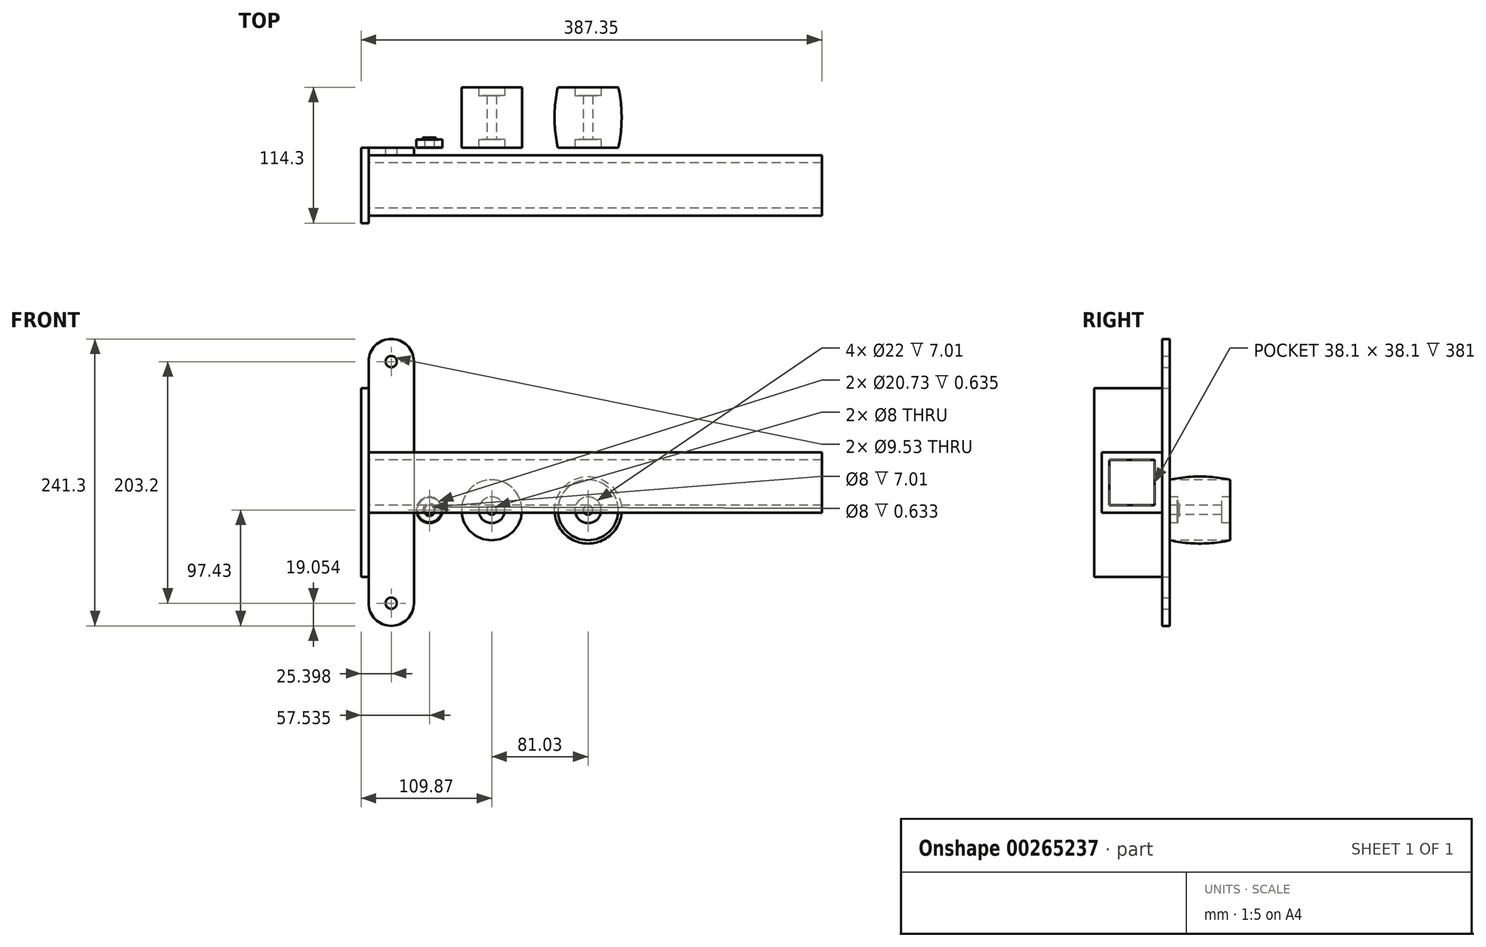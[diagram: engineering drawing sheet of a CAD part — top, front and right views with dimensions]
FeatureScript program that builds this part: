
annotation { "Feature Type Name" : "Feature", "Feature Type Description" : "" }
export const myFeature = defineFeature(function(context is Context, id is Id, definition is map)
    precondition{}
    {
        {
            var Q0;
            Q0=qCreatedBy(makeId("Front.planeOp"),FACE);
            var sketch = newSketch(context, id + "F0", { "sketchPlane" : qUnion([Q0])});
            skLineSegment(sketch, "E0.right", {"start": v(-109.87, -56.15) * mm, "end": v(-109.87, 102.6) * mm});
            skLineSegment(sketch, "E1.left", {"start": v(-109.87, 102.6) * mm, "end": v(-109.87, -56.15) * mm});
            skLineSegment(sketch, "E1.right", {"start": v(-103.52, 102.6) * mm, "end": v(-103.52, -56.15) * mm});
            skLineSegment(sketch, "E2", {"start": v(-103.52, 102.6) * mm, "end": v(-109.87, 102.6) * mm});
            skLineSegment(sketch, "E3", {"start": v(-103.52, -56.15) * mm, "end": v(-109.87, -56.15) * mm});
            skArc(sketch, "E4", {"start": v(-65.42, 124.82) * mm, "mid": v(-84.47, 143.87) * mm, "end": v(-103.52, 124.82) * mm});
            skLineSegment(sketch, "E5", {"start": v(-103.52, 102.6) * mm, "end": v(-103.52, 124.82) * mm});
            skArc(sketch, "E6", {"start": v(-103.52, -78.38) * mm, "mid": v(-84.47, -97.43) * mm, "end": v(-65.42, -78.38) * mm});
            skLineSegment(sketch, "E7", {"start": v(-103.52, -56.15) * mm, "end": v(-103.52, -78.38) * mm});
            skLineSegment(sketch, "E8", {"start": v(-65.42, 124.82) * mm, "end": v(-65.42, -78.38) * mm});
            skSolve(sketch);
        }
        {
            var Q0;
            Q0=makeQuery(id+"F0.imprint","IMPRINT",FACE,{"disambiguationData":[TD([[makeQuery(id+"F0.imprint","IMPRINT",EDGE,{"derivedFrom":sQuery(id+"F0.wireOp",EDGE,"E1.right")}),-1.0]])]});
            extrude(context, id + "F1", {"entities" : qUnion([Q0]), "depth" : 63.5 * mm});
        }
        {
            var Q0;
            Q0=makeQuery(id+"F0.imprint","IMPRINT",FACE,{"disambiguationData":[TD([[makeQuery(id+"F0.imprint","IMPRINT",EDGE,{"derivedFrom":sQuery(id+"F0.wireOp",EDGE,"E1.right")}),1.0]])]});
            extrude(context, id + "F2", {"entities" : qUnion([Q0]), "operationType" : NewBodyOperationType.ADD, "depth" : 6.35 * mm});
        }
        {
            var Q0;
            Q0=sQuery(id+"F0.wireOp",VERTEX,"E6.center");
            var Q1;
            Q1=sQuery(id+"F0.wireOp",VERTEX,"E4.center");
            var Q2;
            Q2=makeQuery(id+"F1.opExtrude","SWEPT_BODY",BODY,{"disambiguationData":[OSD([sQuery(id+"F0.wireOp",EDGE,"E1.bottom"),sQuery(id+"F0.wireOp",EDGE,"E1.top"),sQuery(id+"F0.wireOp",EDGE,"E1.left"),sQuery(id+"F0.wireOp",EDGE,"E1.right")])]});
            hole(context, id + "F3", {"style" : HoleStyle.SIMPLE, "endStyle" : HoleEndStyle.THROUGH, "oppositeDirection" : true, "holeDiameter" : 9.52 * mm, "tappedDepth" : 12.7 * mm, "tapClearance" : 3, "startFromSketch" : true, "locations" : qUnion([Q0, Q1]), "scope" : qUnion([Q2])});
        }
        {
            var Q0;
            Q0=makeQuery(id+"F1.opExtrude","SWEPT_FACE",FACE,{"disambiguationData":[OSD([sQuery(id+"F0.wireOp",EDGE,"E1.right")])]});
            var sketch = newSketch(context, id + "F4", { "sketchPlane" : qUnion([Q0])});
            skLineSegment(sketch, "E9.bottom", {"start": v(-6.35, 48.62) * mm, "end": v(-57.15, 48.62) * mm});
            skLineSegment(sketch, "E9.top", {"start": v(-6.35, -2.18) * mm, "end": v(-57.15, -2.18) * mm});
            skLineSegment(sketch, "E9.left", {"start": v(-6.35, 48.62) * mm, "end": v(-6.35, -2.18) * mm});
            skLineSegment(sketch, "E9.right", {"start": v(-57.15, 48.62) * mm, "end": v(-57.15, -2.18) * mm});
            skLineSegment(sketch, "E10.0", {"start": v(-50.8, 42.27) * mm, "end": v(-50.8, 4.17) * mm});
            skLineSegment(sketch, "E10.1", {"start": v(-12.7, 42.27) * mm, "end": v(-50.8, 42.27) * mm});
            skLineSegment(sketch, "E10.2", {"start": v(-12.7, 42.27) * mm, "end": v(-12.7, 4.17) * mm});
            skLineSegment(sketch, "E10.3", {"start": v(-12.7, 4.17) * mm, "end": v(-50.8, 4.17) * mm});
            skSolve(sketch);
        }
        {
            var Q0;
            Q0 = qSketchRegion(id + "F4", true);
            extrude(context, id + "F5", {"entities" : qUnion([Q0]), "operationType" : NewBodyOperationType.ADD, "depth" : 381 * mm});
        }
        {
            var Q0;
            Q0=qCreatedBy(makeId("Top.planeOp"),FACE);
            var sketch = newSketch(context, id + "F6", { "sketchPlane" : qUnion([Q0])});
            skLineSegment(sketch, "E11", {"start": v(0, 0) * mm, "end": v(0, 108.82) * mm, "construction": true});
            skLineSegment(sketch, "E12", {"start": v(-25.4, 0) * mm, "end": v(-25.4, 50.8) * mm});
            skLineSegment(sketch, "E13", {"start": v(-4, 7.01) * mm, "end": v(-4, 43.79) * mm});
            skLineSegment(sketch, "E14", {"start": v(-11, 0) * mm, "end": v(-11, 7.01) * mm});
            skLineSegment(sketch, "E15", {"start": v(-25.4, 0) * mm, "end": v(-11, 0) * mm});
            skLineSegment(sketch, "E16", {"start": v(-11, 7.01) * mm, "end": v(-4, 7.01) * mm});
            skLineSegment(sketch, "E17", {"start": v(-25.4, 50.8) * mm, "end": v(-11, 50.8) * mm});
            skLineSegment(sketch, "E18", {"start": v(-11, 43.79) * mm, "end": v(-4, 43.79) * mm});
            skPoint(sketch, "E19.orphan", {"position": v(-4, 0) * mm});
            skLineSegment(sketch, "E20.trimOffspring", {"start": v(-11, 43.79) * mm, "end": v(-11, 50.8) * mm});
            skSolve(sketch);
        }
        {
            var Q0;
            Q0 = qSketchRegion(id + "F6", true);
            var Q1;
            Q1=sQuery(id+"F6.wireOp",EDGE,"E11");
            revolve(context, id + "F7", {"entities" : qUnion([Q0]), "axis" : qUnion([Q1]), "revolveType" : RevolveType.FULL});
        }
        {
            var Q0;
            Q0=qCreatedBy(makeId("Top.planeOp"),FACE);
            var sketch = newSketch(context, id + "F8", { "sketchPlane" : qUnion([Q0])});
            skLineSegment(sketch, "E21", {"start": v(81.03, 0) * mm, "end": v(81.03, 50.8) * mm, "construction": true});
            skLineSegment(sketch, "E22", {"start": v(55.63, 0) * mm, "end": v(55.63, 50.8) * mm, "construction": true});
            skLineSegment(sketch, "E23", {"start": v(55.63, 0) * mm, "end": v(70.03, 0) * mm});
            skLineSegment(sketch, "E24", {"start": v(55.63, 50.8) * mm, "end": v(70.03, 50.8) * mm});
            skPoint(sketch, "E25.orphan", {"position": v(55.63, 70.87) * mm});
            skPoint(sketch, "E26.orphan", {"position": v(81.03, 70.87) * mm});
            skPoint(sketch, "E27.endSnap0", {"position": v(81.03, 25.4) * mm});
            skArc(sketch, "E28", {"start": v(55.63, 50.8) * mm, "mid": v(52.84, 25.4) * mm, "end": v(55.63, 0) * mm});
            skPoint(sketch, "E28.third.point", {"position": v(286.5, 28.62) * mm});
            skPoint(sketch, "E29.orphan", {"position": v(55.63, 25.4) * mm});
            skLineSegment(sketch, "E30", {"start": v(70.03, 7.01) * mm, "end": v(77.03, 7.01) * mm});
            skLineSegment(sketch, "E31", {"start": v(77.03, 7.01) * mm, "end": v(77.03, 43.79) * mm});
            skLineSegment(sketch, "E32", {"start": v(77.03, 43.79) * mm, "end": v(70.03, 43.79) * mm});
            skLineSegment(sketch, "E33", {"start": v(70.03, 50.8) * mm, "end": v(70.03, 43.79) * mm});
            skPoint(sketch, "E34.orphan", {"position": v(68.33, 43.79) * mm});
            skPoint(sketch, "E35.orphan", {"position": v(68.33, 7.01) * mm});
            skLineSegment(sketch, "E36.trimOffspring", {"start": v(70.03, 7.01) * mm, "end": v(70.03, 0) * mm});
            skPoint(sketch, "E37.orphan", {"position": v(68.33, 50.8) * mm});
            skPoint(sketch, "E38.orphan", {"position": v(68.33, 0) * mm});
            skSolve(sketch);
        }
        {
            var Q0;
            Q0 = qSketchRegion(id + "F8", true);
            var Q1;
            Q1=sQuery(id+"F8.wireOp",EDGE,"E21");
            revolve(context, id + "F9", {"entities" : qUnion([Q0]), "axis" : qUnion([Q1]), "revolveType" : RevolveType.FULL});
        }
        {
            var Q0;
            Q0=qCreatedBy(makeId("Top.planeOp"),FACE);
            var sketch = newSketch(context, id + "F10", { "sketchPlane" : qUnion([Q0])});
            skLineSegment(sketch, "E39", {"start": v(-52.34, 0) * mm, "end": v(-52.34, 11.8) * mm, "construction": true});
            skLineSegment(sketch, "E40", {"start": v(-56.34, 0) * mm, "end": v(-56.34, 7.01) * mm});
            skLineSegment(sketch, "E41", {"start": v(-63.33, 0) * mm, "end": v(-63.33, 7.01) * mm});
            skLineSegment(sketch, "E42", {"start": v(-63.33, 0) * mm, "end": v(-62.7, 0) * mm});
            skLineSegment(sketch, "E43", {"start": v(-62.7, 0) * mm, "end": v(-62.7, 0.63) * mm});
            skLineSegment(sketch, "E44", {"start": v(-62.7, 0.63) * mm, "end": v(-56.97, 0.63) * mm});
            skLineSegment(sketch, "E45", {"start": v(-56.97, 0.63) * mm, "end": v(-56.97, 0) * mm});
            skLineSegment(sketch, "E46", {"start": v(-56.97, 0) * mm, "end": v(-56.34, 0) * mm});
            skLineSegment(sketch, "E47", {"start": v(-65.2, 3.5) * mm, "end": v(-54.77, 3.5) * mm, "construction": true});
            skLineSegment(sketch, "E48.MirrorCS", {"start": v(-56.97, 7.01) * mm, "end": v(-56.34, 7.01) * mm});
            skLineSegment(sketch, "E49.MirrorCS", {"start": v(-56.97, 6.38) * mm, "end": v(-56.97, 7.01) * mm});
            skLineSegment(sketch, "E50.MirrorCS", {"start": v(-62.7, 6.38) * mm, "end": v(-56.97, 6.38) * mm});
            skLineSegment(sketch, "E51.MirrorCS", {"start": v(-63.33, 7.01) * mm, "end": v(-62.7, 7.01) * mm});
            skLineSegment(sketch, "E52.MirrorCS", {"start": v(-62.7, 7.01) * mm, "end": v(-62.7, 6.38) * mm});
            skPoint(sketch, "E53.orphan", {"position": v(-63.33, 10.85) * mm});
            skPoint(sketch, "E54.orphan", {"position": v(-56.34, 10.85) * mm});
            skLineSegment(sketch, "E55.bottom", {"start": v(-56.34, 7.77) * mm, "end": v(-57.89, 7.77) * mm});
            skLineSegment(sketch, "E55.top", {"start": v(-56.34, 8.4) * mm, "end": v(-57.89, 8.4) * mm});
            skLineSegment(sketch, "E55.left", {"start": v(-56.34, 7.77) * mm, "end": v(-56.34, 8.4) * mm});
            skLineSegment(sketch, "E55.right", {"start": v(-57.89, 7.77) * mm, "end": v(-57.89, 8.4) * mm});
            skSolve(sketch);
        }
        {
            var Q0;
            Q0 = qSketchRegion(id + "F10", true);
            var Q1;
            Q1=sQuery(id+"F10.wireOp",EDGE,"E39");
            revolve(context, id + "F11", {"entities" : qUnion([Q0]), "axis" : qUnion([Q1]), "revolveType" : RevolveType.FULL});
        }
    });
